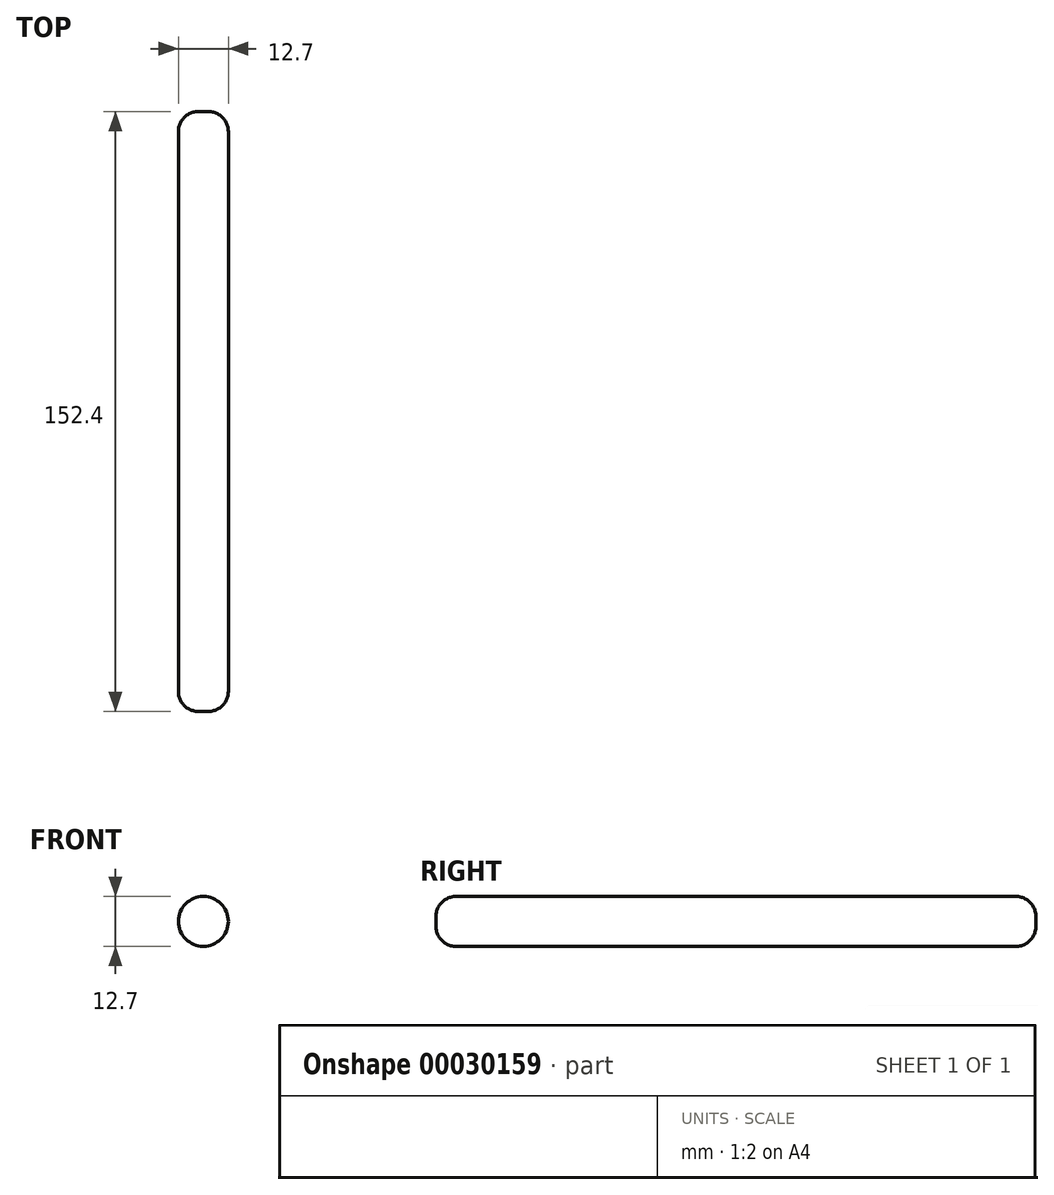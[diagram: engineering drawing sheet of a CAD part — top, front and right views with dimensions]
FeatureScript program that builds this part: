
annotation { "Feature Type Name" : "Feature", "Feature Type Description" : "" }
export const myFeature = defineFeature(function(context is Context, id is Id, definition is map)
    precondition{}
    {
        {
            var Q0;
            Q0=qCreatedBy(makeId("Front.planeOp"),FACE);
            var sketch = newSketch(context, id + "F0", { "sketchPlane" : qUnion([Q0])});
            skCircle(sketch, "E0", {"center": v(0, 0) * mm, "radius": 6.35 * mm});
            skSolve(sketch);
        }
        {
            var Q0;
            Q0 = qSketchRegion(id + "F0", true);
            extrude(context, id + "F1", {"entities" : qUnion([Q0]), "depth" : 152.4 * mm});
        }
        {
            var Q0;
            Q0=makeQuery(id+"F1.opExtrude","CAP_EDGE",EDGE,{"disambiguationData":[OSD([sQuery(id+"F0.wireOp",EDGE,"E0")])],"isStart":true});
            var Q1;
            Q1=makeQuery(id+"F1.opExtrude","CAP_EDGE",EDGE,{"disambiguationData":[OSD([sQuery(id+"F0.wireOp",EDGE,"E0")])],"isStart":false});
            fillet(context, id + "F2", {"entities" : qUnion([Q0, Q1]), "radius" : 5.08 * mm, "tangentPropagation" : true, "allowEdgeOverflow" : false});
        }
    });
